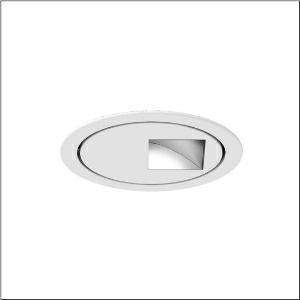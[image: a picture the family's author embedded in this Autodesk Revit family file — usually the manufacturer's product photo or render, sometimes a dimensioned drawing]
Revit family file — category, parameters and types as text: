
# Revit family: lunis_11_mini_round_51dk11b72wf21
name_source: partatom
category: Lighting Fixtures
units: mm (PartAtom-declared; Revit-internal decimal feet)

## family parameters
Cut with Voids When Loaded = No
Host = Face
Light Source = No
Part Type = Normal
Room Calculation Point = No
Round Connector Dimension = Use Diameter
Shared = No

## types (1)
- Lunis 11 mini round (1 x LED 3000K / CRI = 80 (unbekannt), 2380 lm, 3000K)
    Apparent Load = 28 VA
    CIE Flux Codes = 44 77 97 100 100
    Color Rendering = 80
    Color Temperature = 3000K
    Default Elevation = 1800 mm
    Description = Lunis 11 mini round, downlight, light control with wallwasher, of highly reflective aluminium, highly specular, light emission: direct distribution, LED rated luminous flux: 2.380lm, light colour: 830, control gear: ECG, with terminal, 3-pole, mains connection: 220..230V, AC/DC, 0/50..60Hz, LED module, luminaire module, of aluminium, highly specular, white, diameter: 176mm, clamping range: 1..40mm, recessing ring, of plastic, traffic white (RAL 9016), protection rating (complete): IP20, insulation class (complete): insulation class II (safety insulation), certification: CE, permissible ambient temperature for indoor applications: 0..+35°C, packaging unit: 1 piece
    Height = 0 mm  [stored 0 ft]
    Lamp = 1 x LED 3000K / CRI >= 80 (unbekannt)
    Lamp Light Flux = 2380 lm
    Lamp count = 1
    Length = 176 mm
    Luminous efficacy = 85 lm/W
    Manufacturer = Siteco
    ModVariant = No
    Model = 51DK11B72WF21
    Mounting Place = Ceiling
    Mounting Type = Recessed
    Number of Poles = 1
    OnlyDefault = Yes
    Power Factor = 1
    Product Name = Lunis 11 mini round
    Product group = downlight
    ProductGroupID = 400
    Protection Class = Protection class II
    Protection Degree = IP 20
    RLX_Detail_Level = 1
    RLX_Emergency_Light_Flux = 0 lm
    RLX_Emergency_Type = 0
    RLX_Emergency_Type_DB = No
    RlxData = <blob elided: 59277 chars, md5=4376f1a0>
    Socket = socket
    Standby Power = 0 W
    System Light Flux = 2380 lm
    System Power = 28 W
    Type Comments = Product without accessories
    Type Image = l_1004772.jpg
    URL = http://relux.com
    VarID = ---
    Voltage = 0 V
    Weight = 0.00 kg
    Width = 176 mm

note: [stored X ft] marks values corroborated as IEEE doubles in the binary element streams (Revit-internal decimal feet)

## geometry (parser evidence)
native form markers: Blend x4, Sweep x9
no freeform markers — native parametric forms only
